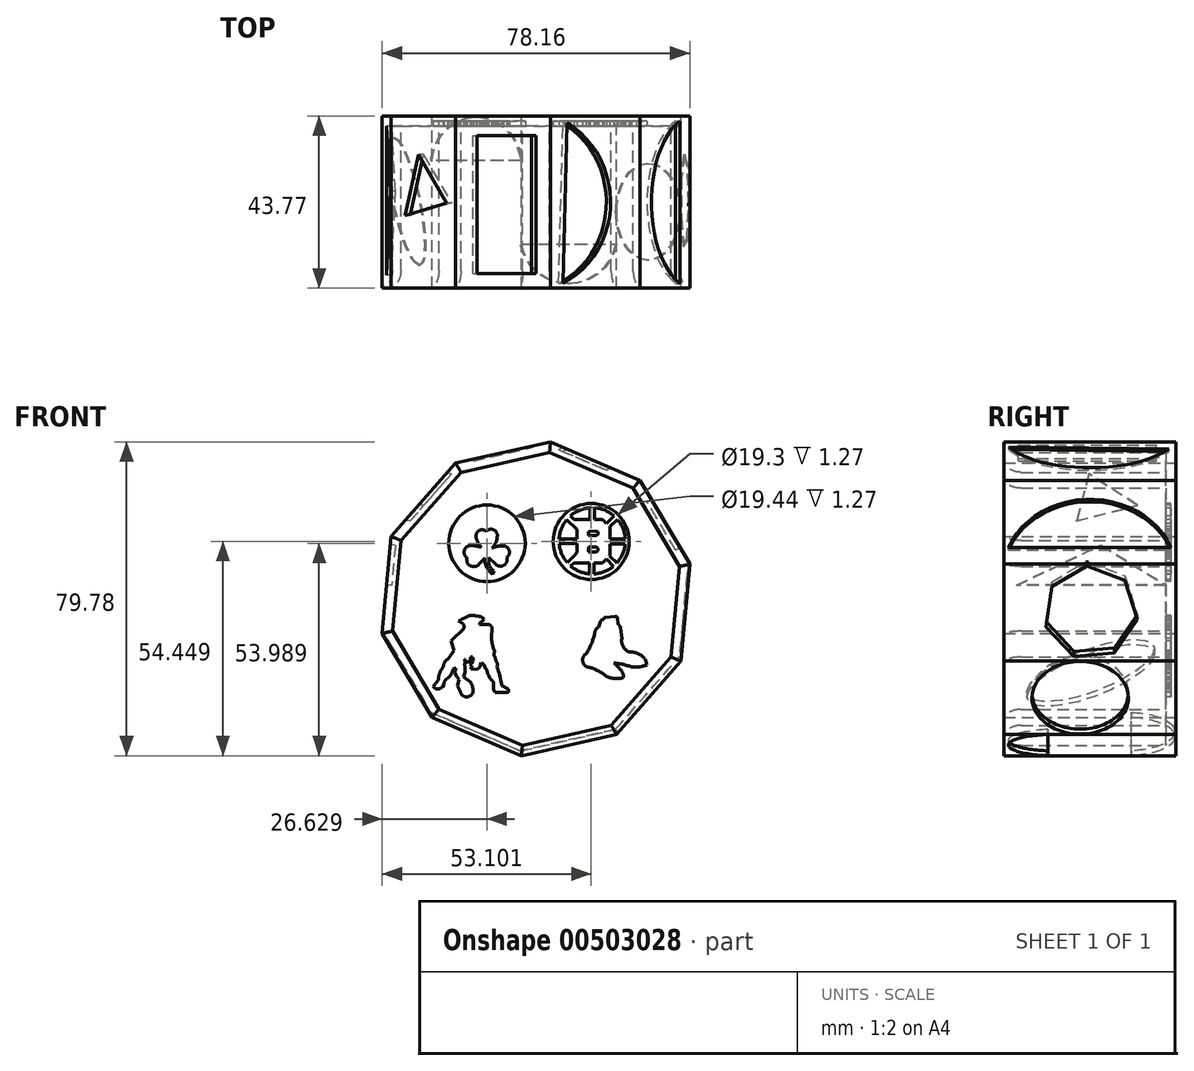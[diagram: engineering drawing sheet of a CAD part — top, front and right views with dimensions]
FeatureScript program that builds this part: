
annotation { "Feature Type Name" : "Feature", "Feature Type Description" : "" }
export const myFeature = defineFeature(function(context is Context, id is Id, definition is map)
    precondition{}
    {
        {
            var Q0;
            Q0=qCreatedBy(makeId("Front.planeOp"),FACE);
            var sketch = newSketch(context, id + "F0", { "sketchPlane" : qUnion([Q0])});
            skCircle(sketch, "E0.cCircle", {"center": v(0, 0) * mm, "radius": 38.1 * mm, "construction": true});
            skLineSegment(sketch, "E0.0", {"start": v(3.7, 39.89) * mm, "end": v(26.44, 30.1) * mm});
            skLineSegment(sketch, "E0.1", {"start": v(26.44, 30.1) * mm, "end": v(39.08, 8.8) * mm});
            skLineSegment(sketch, "E0.2", {"start": v(39.08, 8.8) * mm, "end": v(36.8, -15.85) * mm});
            skLineSegment(sketch, "E0.3", {"start": v(36.8, -15.85) * mm, "end": v(20.45, -34.45) * mm});
            skLineSegment(sketch, "E0.4", {"start": v(20.45, -34.45) * mm, "end": v(-3.7, -39.89) * mm});
            skLineSegment(sketch, "E0.5", {"start": v(-3.7, -39.89) * mm, "end": v(-26.44, -30.1) * mm});
            skLineSegment(sketch, "E0.6", {"start": v(-26.44, -30.1) * mm, "end": v(-39.08, -8.8) * mm});
            skLineSegment(sketch, "E0.7", {"start": v(-39.08, -8.8) * mm, "end": v(-36.8, 15.85) * mm});
            skLineSegment(sketch, "E0.8", {"start": v(-36.8, 15.85) * mm, "end": v(-20.45, 34.45) * mm});
            skLineSegment(sketch, "E0.9", {"start": v(-20.45, 34.45) * mm, "end": v(3.7, 39.89) * mm});
            skPoint(sketch, "E0.0.midPoint", {"position": v(15.07, 35) * mm});
            skSolve(sketch);
        }
        {
            var Q0;
            Q0 = qSketchRegion(id + "F0", true);
            extrude(context, id + "F1", {"entities" : qUnion([Q0]), "depth" : 25.4 * mm, "hasSecondDirection" : true, "secondDirectionOppositeDirection" : true, "secondDirectionDepth" : 12.7 * mm});
        }
        {
            var Q0;
            Q0 = qSketchRegion(id + "F0", true);
            extrude(context, id + "F2", {"entities" : qUnion([Q0]), "operationType" : NewBodyOperationType.ADD, "oppositeDirection" : true, "depth" : 19.05 * mm});
        }
        {
            var Q0;
            Q0=makeQuery(id+"F1.opExtrude","CAP_FACE",FACE,{"disambiguationData":[OSD([sQuery(id+"F0.wireOp",EDGE,"E0.0"),sQuery(id+"F0.wireOp",EDGE,"E0.1"),sQuery(id+"F0.wireOp",EDGE,"E0.2"),sQuery(id+"F0.wireOp",EDGE,"E0.3"),sQuery(id+"F0.wireOp",EDGE,"E0.4"),sQuery(id+"F0.wireOp",EDGE,"E0.5"),sQuery(id+"F0.wireOp",EDGE,"E0.6"),sQuery(id+"F0.wireOp",EDGE,"E0.7"),sQuery(id+"F0.wireOp",EDGE,"E0.8"),sQuery(id+"F0.wireOp",EDGE,"E0.9")])],"isStart":false});
            shell(context, id + "F3", {"entities" : qUnion([Q0]), "thickness" : 2.54 * mm});
        }
        {
            var Q0;
            {var subQ0=sQuery(id+"F0.wireOp",EDGE,"E0.1");Q0=makeQuery(id+"F3.opShell","OFFSET_EDGE",EDGE,{"disambiguationData":[OSD([subQ0]),TDD([makeQuery(id+"F1.opExtrude","CAP_EDGE",EDGE,{"disambiguationData":[OSD([subQ0])],"isStart":false})])]});}
            var Q1;
            {var subQ0=sQuery(id+"F0.wireOp",EDGE,"E0.2");Q1=makeQuery(id+"F3.opShell","OFFSET_EDGE",EDGE,{"disambiguationData":[OSD([subQ0]),TDD([makeQuery(id+"F1.opExtrude","CAP_EDGE",EDGE,{"disambiguationData":[OSD([subQ0])],"isStart":false})])]});}
            var Q2;
            {var subQ0=sQuery(id+"F0.wireOp",EDGE,"E0.3");Q2=makeQuery(id+"F3.opShell","OFFSET_EDGE",EDGE,{"disambiguationData":[OSD([subQ0]),TDD([makeQuery(id+"F1.opExtrude","CAP_EDGE",EDGE,{"disambiguationData":[OSD([subQ0])],"isStart":false})])]});}
            var Q3;
            {var subQ0=sQuery(id+"F0.wireOp",EDGE,"E0.4");Q3=makeQuery(id+"F3.opShell","OFFSET_EDGE",EDGE,{"disambiguationData":[OSD([subQ0]),TDD([makeQuery(id+"F1.opExtrude","CAP_EDGE",EDGE,{"disambiguationData":[OSD([subQ0])],"isStart":false})])]});}
            var Q4;
            {var subQ0=sQuery(id+"F0.wireOp",EDGE,"E0.5");Q4=makeQuery(id+"F3.opShell","OFFSET_EDGE",EDGE,{"disambiguationData":[OSD([subQ0]),TDD([makeQuery(id+"F1.opExtrude","CAP_EDGE",EDGE,{"disambiguationData":[OSD([subQ0])],"isStart":false})])]});}
            var Q5;
            {var subQ0=sQuery(id+"F0.wireOp",EDGE,"E0.0");Q5=makeQuery(id+"F3.opShell","OFFSET_EDGE",EDGE,{"disambiguationData":[OSD([subQ0]),TDD([makeQuery(id+"F1.opExtrude","CAP_EDGE",EDGE,{"disambiguationData":[OSD([subQ0])],"isStart":false})])]});}
            var Q6;
            {var subQ0=sQuery(id+"F0.wireOp",EDGE,"E0.9");Q6=makeQuery(id+"F3.opShell","OFFSET_EDGE",EDGE,{"disambiguationData":[OSD([subQ0]),TDD([makeQuery(id+"F1.opExtrude","CAP_EDGE",EDGE,{"disambiguationData":[OSD([subQ0])],"isStart":false})])]});}
            var Q7;
            {var subQ0=sQuery(id+"F0.wireOp",EDGE,"E0.8");Q7=makeQuery(id+"F3.opShell","OFFSET_EDGE",EDGE,{"disambiguationData":[OSD([subQ0]),TDD([makeQuery(id+"F1.opExtrude","CAP_EDGE",EDGE,{"disambiguationData":[OSD([subQ0])],"isStart":false})])]});}
            var Q8;
            {var subQ0=sQuery(id+"F0.wireOp",EDGE,"E0.7");Q8=makeQuery(id+"F3.opShell","OFFSET_EDGE",EDGE,{"disambiguationData":[OSD([subQ0]),TDD([makeQuery(id+"F1.opExtrude","CAP_EDGE",EDGE,{"disambiguationData":[OSD([subQ0])],"isStart":false})])]});}
            var Q9;
            {var subQ0=sQuery(id+"F0.wireOp",EDGE,"E0.6");Q9=makeQuery(id+"F3.opShell","OFFSET_EDGE",EDGE,{"disambiguationData":[OSD([subQ0]),TDD([makeQuery(id+"F1.opExtrude","CAP_EDGE",EDGE,{"disambiguationData":[OSD([subQ0])],"isStart":false})])]});}
            fillet(context, id + "F4", {"entities" : qUnion([Q0, Q1, Q2, Q3, Q4, Q5, Q6, Q7, Q8, Q9]), "radius" : 5.08 * mm, "tangentPropagation" : true, "allowEdgeOverflow" : false});
        }
        {
            var Q0;
            Q0=makeQuery(id+"F3.opShell","OFFSET_FACE",FACE,{"disambiguationData":[OSD([sQuery(id+"F0.wireOp",EDGE,"E0.0"),sQuery(id+"F0.wireOp",EDGE,"E0.1"),sQuery(id+"F0.wireOp",EDGE,"E0.2"),sQuery(id+"F0.wireOp",EDGE,"E0.3"),sQuery(id+"F0.wireOp",EDGE,"E0.4"),sQuery(id+"F0.wireOp",EDGE,"E0.5"),sQuery(id+"F0.wireOp",EDGE,"E0.6"),sQuery(id+"F0.wireOp",EDGE,"E0.7"),sQuery(id+"F0.wireOp",EDGE,"E0.8"),sQuery(id+"F0.wireOp",EDGE,"E0.9")])]});
            var sketch = newSketch(context, id + "F5", { "sketchPlane" : qUnion([Q0])});
            skCircle(sketch, "E1", {"center": v(-12.45, 14.1) * mm, "radius": 9.72 * mm});
            skPoint(sketch, "E1.first.point", {"position": v(-12.45, 4.38) * mm});
            skPoint(sketch, "E1.first.point.positionSnap0", {"position": v(-12.45, 3.33) * mm});
            skPoint(sketch, "E1.second.point", {"position": v(-12.45, 23.82) * mm});
            skPoint(sketch, "E1.second.point.positionSnap0", {"position": v(-12.45, 3.33) * mm});
            skPoint(sketch, "E1.third.point", {"position": v(-6.09, 21.45) * mm});
            skArc(sketch, "E2", {"start": v(-12.96, 10.41) * mm, "mid": v(-12.53, 8.05) * mm, "end": v(-11, 6.21) * mm});
            skArc(sketch, "E3", {"start": v(-12.12, 10.54) * mm, "mid": v(-11.9, 8.6) * mm, "end": v(-10.73, 7.03) * mm});
            skLineSegment(sketch, "E4", {"start": v(-10.73, 7.03) * mm, "end": v(-11, 6.21) * mm});
            skLineSegment(sketch, "E5", {"start": v(-12.12, 10.54) * mm, "end": v(-10.2, 8.72) * mm});
            skLineSegment(sketch, "E6", {"start": v(-12.96, 10.41) * mm, "end": v(-14.56, 8.72) * mm});
            skArc(sketch, "E7", {"start": v(-10.2, 8.72) * mm, "mid": v(-8.14, 8.53) * mm, "end": v(-7.46, 10.49) * mm});
            skArc(sketch, "E8", {"start": v(-7.46, 10.49) * mm, "mid": v(-6.8, 12.25) * mm, "end": v(-8.24, 13.46) * mm});
            skArc(sketch, "E9", {"start": v(-17.53, 10.41) * mm, "mid": v(-16.7, 8.4) * mm, "end": v(-14.56, 8.72) * mm});
            skArc(sketch, "E10", {"start": v(-16.68, 13.54) * mm, "mid": v(-18.21, 12.28) * mm, "end": v(-17.53, 10.41) * mm});
            skArc(sketch, "E11", {"start": v(-13.8, 13.06) * mm, "mid": v(-15.22, 13.4) * mm, "end": v(-16.68, 13.54) * mm});
            skArc(sketch, "E12", {"start": v(-8.24, 13.46) * mm, "mid": v(-9.78, 13.35) * mm, "end": v(-11.24, 12.85) * mm});
            skArc(sketch, "E13", {"start": v(-11.24, 12.85) * mm, "mid": v(-10.25, 14.25) * mm, "end": v(-9.83, 15.9) * mm});
            skArc(sketch, "E14", {"start": v(-9.83, 15.9) * mm, "mid": v(-10.78, 17.54) * mm, "end": v(-12.63, 17.13) * mm});
            skArc(sketch, "E15", {"start": v(-12.63, 17.13) * mm, "mid": v(-14.36, 17.4) * mm, "end": v(-15.25, 15.9) * mm});
            skArc(sketch, "E16", {"start": v(-15.25, 15.9) * mm, "mid": v(-14.78, 14.35) * mm, "end": v(-13.8, 13.06) * mm});
            skCircle(sketch, "E17", {"center": v(14.02, 14.56) * mm, "radius": 9.65 * mm});
            skPoint(sketch, "E17.first.point", {"position": v(14.6, 4.92) * mm});
            skPoint(sketch, "E17.second.point", {"position": v(14.21, 24.2) * mm});
            skPoint(sketch, "E17.second.point.positionSnap0", {"position": v(14.21, 24.72) * mm});
            skPoint(sketch, "E17.third.point", {"position": v(9.59, 23.13) * mm});
            skArc(sketch, "E18", {"start": v(7.8, 20.1) * mm, "mid": v(6.44, 17.82) * mm, "end": v(5.86, 15.22) * mm});
            skPoint(sketch, "E18.first.point", {"position": v(14.35, 6.3) * mm});
            skPoint(sketch, "E18.second.point", {"position": v(14.02, 23.13) * mm});
            skPoint(sketch, "E18.third.point", {"position": v(9.59, 21.72) * mm});
            skLineSegment(sketch, "E19", {"start": v(10.13, 20.2) * mm, "end": v(9.62, 20.2) * mm});
            skLineSegment(sketch, "E20", {"start": v(9.62, 18.37) * mm, "end": v(10.39, 17.63) * mm});
            skLineSegment(sketch, "E21", {"start": v(9.62, 10.82) * mm, "end": v(10.4, 11.72) * mm});
            skLineSegment(sketch, "E22", {"start": v(9.62, 10.82) * mm, "end": v(7.93, 9.18) * mm});
            skLineSegment(sketch, "E23", {"start": v(9.62, 9.13) * mm, "end": v(13.6, 9.13) * mm});
            skLineSegment(sketch, "E24", {"start": v(8.76, 8.35) * mm, "end": v(9.62, 9.13) * mm});
            skLineSegment(sketch, "E25", {"start": v(13.6, 9.13) * mm, "end": v(13.6, 6.33) * mm});
            skLineSegment(sketch, "E26", {"start": v(14.78, 9.13) * mm, "end": v(14.78, 6.3) * mm});
            skLineSegment(sketch, "E27", {"start": v(14.78, 9.13) * mm, "end": v(16.9, 9.13) * mm});
            skLineSegment(sketch, "E28", {"start": v(16.9, 9.13) * mm, "end": v(17.87, 10.09) * mm});
            skLineSegment(sketch, "E29", {"start": v(17.87, 10.09) * mm, "end": v(19.68, 8.28) * mm});
            skLineSegment(sketch, "E30", {"start": v(20.59, 9.16) * mm, "end": v(18.72, 10.83) * mm});
            skLineSegment(sketch, "E31", {"start": v(18.72, 10.83) * mm, "end": v(18.82, 11.3) * mm});
            skLineSegment(sketch, "E32", {"start": v(18.82, 11.3) * mm, "end": v(18.82, 13.9) * mm});
            skLineSegment(sketch, "E33", {"start": v(18.82, 13.9) * mm, "end": v(18.3, 14.52) * mm});
            skLineSegment(sketch, "E34", {"start": v(18.3, 14.52) * mm, "end": v(18.82, 15.24) * mm});
            skLineSegment(sketch, "E35", {"start": v(18.82, 15.24) * mm, "end": v(22.67, 15.24) * mm});
            skLineSegment(sketch, "E36", {"start": v(22.64, 13.9) * mm, "end": v(18.82, 13.9) * mm});
            skLineSegment(sketch, "E37", {"start": v(18.82, 15.24) * mm, "end": v(18.82, 18.34) * mm});
            skLineSegment(sketch, "E38", {"start": v(18.82, 18.34) * mm, "end": v(20.66, 20.2) * mm});
            skLineSegment(sketch, "E39", {"start": v(17.96, 19.18) * mm, "end": v(16.9, 20.2) * mm});
            skLineSegment(sketch, "E40", {"start": v(17.96, 19.18) * mm, "end": v(19.77, 21.09) * mm});
            skLineSegment(sketch, "E41", {"start": v(10.13, 20.2) * mm, "end": v(13.67, 20.2) * mm});
            skLineSegment(sketch, "E42", {"start": v(13.67, 20.2) * mm, "end": v(13.67, 23.11) * mm});
            skLineSegment(sketch, "E43", {"start": v(14.83, 20.2) * mm, "end": v(14.83, 23.12) * mm});
            skLineSegment(sketch, "E44", {"start": v(14.83, 20.2) * mm, "end": v(16.9, 20.2) * mm});
            skLineSegment(sketch, "E45", {"start": v(10.4, 11.72) * mm, "end": v(10.4, 14) * mm});
            skLineSegment(sketch, "E46", {"start": v(10.4, 14) * mm, "end": v(5.88, 14) * mm});
            skLineSegment(sketch, "E47", {"start": v(10.39, 17.63) * mm, "end": v(10.39, 15.22) * mm});
            skLineSegment(sketch, "E48", {"start": v(10.39, 15.22) * mm, "end": v(5.86, 15.22) * mm});
            skLineSegment(sketch, "E49", {"start": v(9.62, 18.37) * mm, "end": v(7.8, 20.1) * mm});
            skLineSegment(sketch, "E50", {"start": v(9.62, 20.2) * mm, "end": v(8.75, 21.08) * mm});
            skLineSegment(sketch, "E51", {"start": v(13.3, 17.14) * mm, "end": v(13.3, 16.12) * mm});
            skLineSegment(sketch, "E52", {"start": v(13.3, 16.12) * mm, "end": v(15.37, 16.12) * mm});
            skLineSegment(sketch, "E53", {"start": v(15.37, 16.12) * mm, "end": v(15.68, 16.34) * mm});
            skLineSegment(sketch, "E54", {"start": v(15.68, 16.34) * mm, "end": v(15.68, 16.92) * mm});
            skLineSegment(sketch, "E55", {"start": v(15.68, 16.92) * mm, "end": v(15.37, 17.17) * mm});
            skLineSegment(sketch, "E56", {"start": v(15.37, 17.17) * mm, "end": v(13.3, 17.14) * mm});
            skLineSegment(sketch, "E57", {"start": v(13.3, 13.11) * mm, "end": v(13.3, 11.92) * mm});
            skLineSegment(sketch, "E58", {"start": v(13.3, 11.92) * mm, "end": v(15.37, 11.92) * mm});
            skLineSegment(sketch, "E59", {"start": v(15.37, 11.92) * mm, "end": v(15.7, 12.24) * mm});
            skLineSegment(sketch, "E60", {"start": v(15.7, 12.24) * mm, "end": v(15.7, 12.8) * mm});
            skLineSegment(sketch, "E61", {"start": v(15.7, 12.8) * mm, "end": v(15.37, 13.11) * mm});
            skLineSegment(sketch, "E62", {"start": v(15.37, 13.11) * mm, "end": v(13.3, 13.11) * mm});
            skArc(sketch, "E63.trimOffspring", {"start": v(13.67, 23.11) * mm, "mid": v(11.05, 22.5) * mm, "end": v(8.75, 21.08) * mm});
            skArc(sketch, "E64.trimOffspring", {"start": v(5.88, 14) * mm, "mid": v(6.52, 11.42) * mm, "end": v(7.93, 9.18) * mm});
            skArc(sketch, "E65.trimOffspring", {"start": v(8.76, 8.35) * mm, "mid": v(11.02, 6.95) * mm, "end": v(13.6, 6.33) * mm});
            skArc(sketch, "E66.trimOffspring", {"start": v(19.77, 21.09) * mm, "mid": v(17.47, 22.5) * mm, "end": v(14.83, 23.12) * mm});
            skArc(sketch, "E67.trimOffspring", {"start": v(22.67, 15.24) * mm, "mid": v(22.07, 17.88) * mm, "end": v(20.66, 20.2) * mm});
            skArc(sketch, "E68.trimOffspring", {"start": v(20.59, 9.16) * mm, "mid": v(21.99, 11.37) * mm, "end": v(22.64, 13.9) * mm});
            skArc(sketch, "E69.trimOffspring", {"start": v(14.78, 6.32) * mm, "mid": v(17.39, 6.9) * mm, "end": v(19.68, 8.28) * mm});
            skLineSegment(sketch, "E70", {"start": v(16.41, -5.7) * mm, "end": v(15.81, -7.24) * mm});
            skArc(sketch, "E71", {"start": v(15.81, -7.24) * mm, "mid": v(15.13, -7.94) * mm, "end": v(14.89, -8.89) * mm});
            skArc(sketch, "E72", {"start": v(12.7, -14.01) * mm, "mid": v(14.03, -11.55) * mm, "end": v(14.89, -8.89) * mm});
            skArc(sketch, "E73", {"start": v(12.7, -14.01) * mm, "mid": v(11.91, -16.14) * mm, "end": v(13.75, -17.45) * mm});
            skArc(sketch, "E74", {"start": v(17.1, -19.09) * mm, "mid": v(15.49, -18.14) * mm, "end": v(13.75, -17.45) * mm});
            skArc(sketch, "E75", {"start": v(17.1, -19.09) * mm, "mid": v(19.53, -20.22) * mm, "end": v(22.2, -19.98) * mm});
            skArc(sketch, "E76", {"start": v(22.2, -19.98) * mm, "mid": v(22.06, -18.92) * mm, "end": v(21.47, -18.04) * mm});
            skArc(sketch, "E77", {"start": v(21.47, -18.04) * mm, "mid": v(20.68, -17.15) * mm, "end": v(19.84, -16.32) * mm});
            skArc(sketch, "E78", {"start": v(24.23, -17.32) * mm, "mid": v(22.07, -16.66) * mm, "end": v(19.84, -16.32) * mm});
            skArc(sketch, "E79", {"start": v(24.23, -17.32) * mm, "mid": v(26.23, -17.31) * mm, "end": v(28.17, -16.79) * mm});
            skArc(sketch, "E80", {"start": v(28.17, -16.79) * mm, "mid": v(27.31, -14.91) * mm, "end": v(25.57, -13.8) * mm});
            skArc(sketch, "E81", {"start": v(25.57, -13.8) * mm, "mid": v(24.78, -13.58) * mm, "end": v(23.95, -13.55) * mm});
            skArc(sketch, "E82", {"start": v(21.8, -10.12) * mm, "mid": v(22.18, -12.27) * mm, "end": v(23.95, -13.55) * mm});
            skLineSegment(sketch, "E83", {"start": v(21.8, -10.12) * mm, "end": v(21.46, -7.43) * mm});
            skArc(sketch, "E84", {"start": v(21.46, -7.43) * mm, "mid": v(21.24, -6.87) * mm, "end": v(20.79, -6.47) * mm});
            skLineSegment(sketch, "E85", {"start": v(20.03, -4.46) * mm, "end": v(17.66, -4.69) * mm});
            skArc(sketch, "E86", {"start": v(17.66, -4.69) * mm, "mid": v(17.35, -4.86) * mm, "end": v(17.25, -5.2) * mm});
            skArc(sketch, "E87", {"start": v(17.25, -5.2) * mm, "mid": v(16.75, -5.31) * mm, "end": v(16.41, -5.7) * mm});
            skArc(sketch, "E88", {"start": v(20.7, -4.8) * mm, "mid": v(20.41, -4.53) * mm, "end": v(20.03, -4.46) * mm});
            skLineSegment(sketch, "E89", {"start": v(20.7, -4.8) * mm, "end": v(20.79, -6.47) * mm});
            skArc(sketch, "E90", {"start": v(-19.24, -23.65) * mm, "mid": v(-17.11, -24.86) * mm, "end": v(-16.08, -22.63) * mm});
            skArc(sketch, "E91", {"start": v(-16.08, -22.63) * mm, "mid": v(-16.21, -22.05) * mm, "end": v(-16.56, -21.56) * mm});
            skLineSegment(sketch, "E92", {"start": v(-18.45, -19.84) * mm, "end": v(-16.56, -21.24) * mm});
            skLineSegment(sketch, "E93", {"start": v(-16.56, -21.56) * mm, "end": v(-16.56, -21.24) * mm});
            skLineSegment(sketch, "E94", {"start": v(-18.45, -19.84) * mm, "end": v(-18.07, -18.71) * mm});
            skLineSegment(sketch, "E95", {"start": v(-18.07, -18.71) * mm, "end": v(-18.07, -17.04) * mm});
            skArc(sketch, "E96", {"start": v(-18.07, -16.5) * mm, "mid": v(-18.2, -16.77) * mm, "end": v(-18.07, -17.04) * mm});
            skArc(sketch, "E97", {"start": v(-18.07, -16.5) * mm, "mid": v(-18.03, -15.8) * mm, "end": v(-18.33, -15.16) * mm});
            skLineSegment(sketch, "E98", {"start": v(-18.17, -15.41) * mm, "end": v(-18.06, -15.41) * mm});
            skLineSegment(sketch, "E99", {"start": v(-18.06, -15.41) * mm, "end": v(-17.86, -16.04) * mm});
            skLineSegment(sketch, "E100", {"start": v(-17.86, -16.04) * mm, "end": v(-16.76, -16.08) * mm});
            skLineSegment(sketch, "E101", {"start": v(-16.76, -16.08) * mm, "end": v(-16.64, -14.71) * mm});
            skLineSegment(sketch, "E102", {"start": v(-16.64, -14.71) * mm, "end": v(-16.11, -14.73) * mm});
            skLineSegment(sketch, "E103", {"start": v(-16.11, -14.73) * mm, "end": v(-15.83, -15.84) * mm});
            skLineSegment(sketch, "E104", {"start": v(-15.83, -15.84) * mm, "end": v(-16.7, -16.75) * mm});
            skLineSegment(sketch, "E105", {"start": v(-16.7, -16.75) * mm, "end": v(-16.7, -16.99) * mm});
            skLineSegment(sketch, "E106", {"start": v(-16.7, -16.99) * mm, "end": v(-16.26, -16.99) * mm});
            skLineSegment(sketch, "E107", {"start": v(-16.26, -16.99) * mm, "end": v(-16.54, -17.63) * mm});
            skLineSegment(sketch, "E108", {"start": v(-16.54, -17.63) * mm, "end": v(-16.54, -17.83) * mm});
            skLineSegment(sketch, "E109", {"start": v(-16.54, -17.83) * mm, "end": v(-14.98, -17.98) * mm});
            skLineSegment(sketch, "E110", {"start": v(-14.98, -17.98) * mm, "end": v(-14.26, -17.3) * mm});
            skLineSegment(sketch, "E111", {"start": v(-14.26, -17.3) * mm, "end": v(-14.2, -16.99) * mm});
            skLineSegment(sketch, "E112", {"start": v(-14.2, -16.99) * mm, "end": v(-13.82, -16.36) * mm});
            skLineSegment(sketch, "E113", {"start": v(-13.82, -16.36) * mm, "end": v(-13.62, -16.42) * mm});
            skLineSegment(sketch, "E114", {"start": v(-13.62, -16.42) * mm, "end": v(-13.03, -16.99) * mm});
            skLineSegment(sketch, "E115", {"start": v(-13.03, -16.99) * mm, "end": v(-12.95, -17.59) * mm});
            skLineSegment(sketch, "E116", {"start": v(-12.95, -17.59) * mm, "end": v(-12.47, -18.05) * mm});
            skArc(sketch, "E117", {"start": v(-12.47, -18.05) * mm, "mid": v(-11.9, -19.79) * mm, "end": v(-10.74, -21.2) * mm});
            skLineSegment(sketch, "E118", {"start": v(-10.74, -21.2) * mm, "end": v(-10.74, -23.08) * mm});
            skLineSegment(sketch, "E119", {"start": v(-10.74, -23.08) * mm, "end": v(-10.37, -23.77) * mm});
            skLineSegment(sketch, "E120", {"start": v(-10.37, -23.77) * mm, "end": v(-7.13, -23.77) * mm});
            skArc(sketch, "E121", {"start": v(-7.13, -23.77) * mm, "mid": v(-6.95, -23.36) * mm, "end": v(-7.13, -22.96) * mm});
            skLineSegment(sketch, "E122", {"start": v(-7.13, -22.96) * mm, "end": v(-8.72, -22.06) * mm});
            skArc(sketch, "E123", {"start": v(-8.72, -22.06) * mm, "mid": v(-9.17, -19.68) * mm, "end": v(-9.94, -17.38) * mm});
            skLineSegment(sketch, "E124", {"start": v(-9.94, -17.38) * mm, "end": v(-9.73, -16.72) * mm});
            skArc(sketch, "E125", {"start": v(-10.44, -14.73) * mm, "mid": v(-10.14, -15.74) * mm, "end": v(-9.73, -16.72) * mm});
            skArc(sketch, "E126", {"start": v(-10.44, -14.73) * mm, "mid": v(-11.29, -14.19) * mm, "end": v(-12.24, -14.49) * mm});
            skArc(sketch, "E127", {"start": v(-10.44, -13.45) * mm, "mid": v(-10.68, -13.93) * mm, "end": v(-10.67, -14.47) * mm});
            skArc(sketch, "E128", {"start": v(-11.27, -9.18) * mm, "mid": v(-11.15, -11.37) * mm, "end": v(-10.44, -13.45) * mm});
            skLineSegment(sketch, "E129", {"start": v(-11.27, -9.18) * mm, "end": v(-11.18, -8.06) * mm});
            skArc(sketch, "E130", {"start": v(-11.18, -8.06) * mm, "mid": v(-11.48, -6.86) * mm, "end": v(-12.67, -6.52) * mm});
            skLineSegment(sketch, "E131", {"start": v(-12.67, -6.52) * mm, "end": v(-14.3, -6.52) * mm});
            skLineSegment(sketch, "E132", {"start": v(-14.3, -6.52) * mm, "end": v(-14.3, -6.28) * mm});
            skLineSegment(sketch, "E133", {"start": v(-14.3, -6.28) * mm, "end": v(-13.2, -5.22) * mm});
            skArc(sketch, "E134", {"start": v(-13.2, -5.22) * mm, "mid": v(-14, -4.6) * mm, "end": v(-15.02, -4.44) * mm});
            skArc(sketch, "E135", {"start": v(-15.02, -4.44) * mm, "mid": v(-16.48, -4.2) * mm, "end": v(-17.85, -4.75) * mm});
            skArc(sketch, "E136", {"start": v(-17.85, -4.75) * mm, "mid": v(-18.78, -5.16) * mm, "end": v(-19.66, -5.65) * mm});
            skArc(sketch, "E137", {"start": v(-18.26, -6.74) * mm, "mid": v(-18.9, -6.13) * mm, "end": v(-19.66, -5.65) * mm});
            skLineSegment(sketch, "E138", {"start": v(-18.26, -6.74) * mm, "end": v(-18.26, -7.53) * mm});
            skLineSegment(sketch, "E139", {"start": v(-18.26, -7.53) * mm, "end": v(-21.61, -10.76) * mm});
            skLineSegment(sketch, "E140", {"start": v(-21.61, -10.76) * mm, "end": v(-20.89, -13.1) * mm});
            skLineSegment(sketch, "E141", {"start": v(-20.89, -13.1) * mm, "end": v(-22.18, -15.16) * mm});
            skArc(sketch, "E142", {"start": v(-22.18, -15.16) * mm, "mid": v(-23.19, -16.11) * mm, "end": v(-23.58, -17.44) * mm});
            skArc(sketch, "E143", {"start": v(-23.58, -17.44) * mm, "mid": v(-24.52, -18.92) * mm, "end": v(-24.72, -20.67) * mm});
            skLineSegment(sketch, "E144", {"start": v(-24.72, -20.67) * mm, "end": v(-26.15, -22.34) * mm});
            skArc(sketch, "E145", {"start": v(-26.18, -22.24) * mm, "mid": v(-25.03, -22.91) * mm, "end": v(-23.82, -22.34) * mm});
            skLineSegment(sketch, "E146", {"start": v(-23.82, -22.34) * mm, "end": v(-23.4, -21.77) * mm});
            skArc(sketch, "E147", {"start": v(-22.45, -20.2) * mm, "mid": v(-23.15, -20.85) * mm, "end": v(-23.4, -21.77) * mm});
            skArc(sketch, "E148", {"start": v(-22.45, -20.2) * mm, "mid": v(-21.54, -19.13) * mm, "end": v(-21.05, -17.8) * mm});
            skLineSegment(sketch, "E149", {"start": v(-21.05, -17.8) * mm, "end": v(-20.32, -17.62) * mm});
            skLineSegment(sketch, "E150", {"start": v(-20.32, -17.62) * mm, "end": v(-20.75, -18.67) * mm});
            skLineSegment(sketch, "E151", {"start": v(-20.75, -18.67) * mm, "end": v(-20.08, -19.84) * mm});
            skLineSegment(sketch, "E152", {"start": v(-20.08, -19.84) * mm, "end": v(-19.62, -20.47) * mm});
            skLineSegment(sketch, "E153", {"start": v(-19.62, -20.47) * mm, "end": v(-19.98, -22.17) * mm});
            skLineSegment(sketch, "E154", {"start": v(-19.98, -22.17) * mm, "end": v(-19.24, -23.65) * mm});
            skSolve(sketch);
        }
        {
            var Q0;
            Q0 = qSketchRegion(id + "F5", true);
            extrude(context, id + "F6", {"entities" : qUnion([Q0]), "operationType" : NewBodyOperationType.REMOVE, "oppositeDirection" : true, "depth" : 1.27 * mm});
        }
        {
            var Q0;
            {var subQ0=sQuery(id+"F0.wireOp",EDGE,"E0.4");Q0=makeQuery(id+"F2.boolean.opBoolean","MERGE",FACE,{"derivedFrom":[makeQuery(id+"F1.opExtrude","SWEPT_FACE",FACE,{"disambiguationData":[OSD([subQ0])]}),makeQuery(id+"F2.opExtrude","SWEPT_FACE",FACE,{"disambiguationData":[OSD([subQ0])]})]});}
            var sketch = newSketch(context, id + "F7", { "sketchPlane" : qUnion([Q0])});
            skArc(sketch, "E155", {"start": v(12.38, 13.42) * mm, "mid": v(0, 23.54) * mm, "end": v(-12.38, 13.42) * mm});
            skLineSegment(sketch, "E156", {"start": v(-12.38, 13.42) * mm, "end": v(12.38, 13.42) * mm});
            skSolve(sketch);
        }
        {
            var Q0;
            {var subQ0=sQuery(id+"F0.wireOp",EDGE,"E0.3");Q0=makeQuery(id+"F2.boolean.opBoolean","MERGE",FACE,{"derivedFrom":[makeQuery(id+"F1.opExtrude","SWEPT_FACE",FACE,{"disambiguationData":[OSD([subQ0])]}),makeQuery(id+"F2.opExtrude","SWEPT_FACE",FACE,{"disambiguationData":[OSD([subQ0])]})]});}
            var sketch = newSketch(context, id + "F8", { "sketchPlane" : qUnion([Q0])});
            skCircle(sketch, "E157", {"center": v(-5.27, 0) * mm, "radius": 12.27 * mm});
            skSolve(sketch);
        }
        {
            var Q0;
            {var subQ0=sQuery(id+"F0.wireOp",EDGE,"E0.2");Q0=makeQuery(id+"F2.boolean.opBoolean","MERGE",FACE,{"derivedFrom":[makeQuery(id+"F1.opExtrude","SWEPT_FACE",FACE,{"disambiguationData":[OSD([subQ0])]}),makeQuery(id+"F2.opExtrude","SWEPT_FACE",FACE,{"disambiguationData":[OSD([subQ0])]})]});}
            var sketch = newSketch(context, id + "F9", { "sketchPlane" : qUnion([Q0])});
            skCircle(sketch, "E158.cCircle", {"center": v(-2.58, 0) * mm, "radius": 10.74 * mm, "construction": true});
            skLineSegment(sketch, "E158.0", {"start": v(-13.94, -3.6) * mm, "end": v(-12.47, 6.64) * mm});
            skLineSegment(sketch, "E158.1", {"start": v(-12.47, 6.64) * mm, "end": v(-3.56, 11.88) * mm});
            skLineSegment(sketch, "E158.2", {"start": v(-3.56, 11.88) * mm, "end": v(6.1, 8.17) * mm});
            skLineSegment(sketch, "E158.3", {"start": v(6.1, 8.17) * mm, "end": v(9.22, -1.69) * mm});
            skLineSegment(sketch, "E158.4", {"start": v(9.22, -1.69) * mm, "end": v(3.46, -10.28) * mm});
            skLineSegment(sketch, "E158.5", {"start": v(3.46, -10.28) * mm, "end": v(-6.85, -11.12) * mm});
            skLineSegment(sketch, "E158.6", {"start": v(-6.85, -11.12) * mm, "end": v(-13.94, -3.6) * mm});
            skPoint(sketch, "E158.0.midPoint", {"position": v(-13.2, 1.52) * mm});
            skSolve(sketch);
        }
        {
            var Q0;
            {var subQ0=sQuery(id+"F0.wireOp",EDGE,"E0.1");Q0=makeQuery(id+"F2.boolean.opBoolean","MERGE",FACE,{"derivedFrom":[makeQuery(id+"F1.opExtrude","SWEPT_FACE",FACE,{"disambiguationData":[OSD([subQ0])]}),makeQuery(id+"F2.opExtrude","SWEPT_FACE",FACE,{"disambiguationData":[OSD([subQ0])]})]});}
            var sketch = newSketch(context, id + "F10", { "sketchPlane" : qUnion([Q0])});
            skArc(sketch, "E159", {"start": v(17.8, -7.44) * mm, "mid": v(-2.83, 6.79) * mm, "end": v(-23.47, -7.44) * mm});
            skLineSegment(sketch, "E160", {"start": v(-23.47, -7.44) * mm, "end": v(17.8, -7.44) * mm});
            skSolve(sketch);
        }
        {
            var Q0;
            {var subQ0=sQuery(id+"F0.wireOp",EDGE,"E0.0");Q0=makeQuery(id+"F2.boolean.opBoolean","MERGE",FACE,{"derivedFrom":[makeQuery(id+"F1.opExtrude","SWEPT_FACE",FACE,{"disambiguationData":[OSD([subQ0])]}),makeQuery(id+"F2.opExtrude","SWEPT_FACE",FACE,{"disambiguationData":[OSD([subQ0])]})]});}
            var sketch = newSketch(context, id + "F11", { "sketchPlane" : qUnion([Q0])});
            skArc(sketch, "E161", {"start": v(-8.94, -23.45) * mm, "mid": v(4.2, -3.48) * mm, "end": v(-7.78, 17.2) * mm});
            skLineSegment(sketch, "E162", {"start": v(-8.94, -23.45) * mm, "end": v(-7.78, 17.2) * mm});
            skSolve(sketch);
        }
        {
            var Q0;
            {var subQ0=sQuery(id+"F0.wireOp",EDGE,"E0.9");Q0=makeQuery(id+"F2.boolean.opBoolean","MERGE",FACE,{"derivedFrom":[makeQuery(id+"F1.opExtrude","SWEPT_FACE",FACE,{"disambiguationData":[OSD([subQ0])]}),makeQuery(id+"F2.opExtrude","SWEPT_FACE",FACE,{"disambiguationData":[OSD([subQ0])]})]});}
            var sketch = newSketch(context, id + "F12", { "sketchPlane" : qUnion([Q0])});
            skLineSegment(sketch, "E163.bottom", {"start": v(-6.77, -20.98) * mm, "end": v(8.56, -20.98) * mm});
            skLineSegment(sketch, "E163.top", {"start": v(-6.77, 14.08) * mm, "end": v(8.56, 14.08) * mm});
            skLineSegment(sketch, "E163.left", {"start": v(-6.77, -20.98) * mm, "end": v(-6.77, 14.08) * mm});
            skLineSegment(sketch, "E163.right", {"start": v(8.56, -20.98) * mm, "end": v(8.56, 14.08) * mm});
            skSolve(sketch);
        }
        {
            var Q0;
            {var subQ0=sQuery(id+"F0.wireOp",EDGE,"E0.8");Q0=makeQuery(id+"F2.boolean.opBoolean","MERGE",FACE,{"derivedFrom":[makeQuery(id+"F1.opExtrude","SWEPT_FACE",FACE,{"disambiguationData":[OSD([subQ0])]}),makeQuery(id+"F2.opExtrude","SWEPT_FACE",FACE,{"disambiguationData":[OSD([subQ0])]})]});}
            var sketch = newSketch(context, id + "F13", { "sketchPlane" : qUnion([Q0])});
            skCircle(sketch, "E164.cCircle", {"center": v(0, 0) * mm, "radius": 4.7 * mm, "construction": true});
            skLineSegment(sketch, "E164.0", {"start": v(-9.2, -1.83) * mm, "end": v(3.02, 8.88) * mm});
            skLineSegment(sketch, "E164.1", {"start": v(3.02, 8.88) * mm, "end": v(6.18, -7.06) * mm});
            skLineSegment(sketch, "E164.2", {"start": v(6.18, -7.06) * mm, "end": v(-9.2, -1.83) * mm});
            skPoint(sketch, "E164.0.midPoint", {"position": v(-3.1, 3.53) * mm});
            skSolve(sketch);
        }
        {
            var Q0;
            {var subQ0=sQuery(id+"F0.wireOp",EDGE,"E0.7");Q0=makeQuery(id+"F2.boolean.opBoolean","MERGE",FACE,{"derivedFrom":[makeQuery(id+"F1.opExtrude","SWEPT_FACE",FACE,{"disambiguationData":[OSD([subQ0])]}),makeQuery(id+"F2.opExtrude","SWEPT_FACE",FACE,{"disambiguationData":[OSD([subQ0])]})]});}
            var sketch = newSketch(context, id + "F14", { "sketchPlane" : qUnion([Q0])});
            skLineSegment(sketch, "E165", {"start": v(-16.43, 0) * mm, "end": v(21.34, 0) * mm});
            skLineSegment(sketch, "E166", {"start": v(21.34, 0) * mm, "end": v(0, 10.22) * mm});
            skLineSegment(sketch, "E167", {"start": v(0, 10.22) * mm, "end": v(-16.43, 0) * mm});
            skSolve(sketch);
        }
        {
            var Q0;
            {var subQ0=sQuery(id+"F0.wireOp",EDGE,"E0.6");Q0=makeQuery(id+"F2.boolean.opBoolean","MERGE",FACE,{"derivedFrom":[makeQuery(id+"F1.opExtrude","SWEPT_FACE",FACE,{"disambiguationData":[OSD([subQ0])]}),makeQuery(id+"F2.opExtrude","SWEPT_FACE",FACE,{"disambiguationData":[OSD([subQ0])]})]});}
            var sketch = newSketch(context, id + "F15", { "sketchPlane" : qUnion([Q0])});
            skEllipse(sketch, "E168", {"center": v(2.63, 0) * mm, "majorRadius": 17.56 * mm, "minorRadius": 6.12 * mm, "majorAxis": v(-0.9, 0.42)});
            skSolve(sketch);
        }
        {
            var Q0;
            {var subQ0=sQuery(id+"F0.wireOp",EDGE,"E0.5");Q0=makeQuery(id+"F2.boolean.opBoolean","MERGE",FACE,{"derivedFrom":[makeQuery(id+"F1.opExtrude","SWEPT_FACE",FACE,{"disambiguationData":[OSD([subQ0])]}),makeQuery(id+"F2.opExtrude","SWEPT_FACE",FACE,{"disambiguationData":[OSD([subQ0])]})]});}
            var sketch = newSketch(context, id + "F16", { "sketchPlane" : qUnion([Q0])});
            skLineSegment(sketch, "E169", {"start": v(12.38, -7.7) * mm, "end": v(-12.38, -7.7) * mm});
            skArc(sketch, "E170", {"start": v(-12.38, -7.7) * mm, "mid": v(0, -18.8) * mm, "end": v(12.38, -7.7) * mm});
            skSolve(sketch);
        }
        {
            var Q0;
            Q0 = qSketchRegion(id + "F7", true);
            var Q1;
            Q1 = qSketchRegion(id + "F8", true);
            var Q2;
            Q2 = qSketchRegion(id + "F16", true);
            var Q3;
            Q3 = qSketchRegion(id + "F15", true);
            var Q4;
            Q4 = qSketchRegion(id + "F9", true);
            extrude(context, id + "F17", {"entities" : qUnion([Q0, Q1, Q2, Q3, Q4]), "operationType" : NewBodyOperationType.REMOVE, "oppositeDirection" : true, "depth" : 1.27 * mm});
        }
        {
            var Q0;
            Q0 = qSketchRegion(id + "F10", true);
            var Q1;
            Q1 = qSketchRegion(id + "F11", true);
            var Q2;
            Q2 = qSketchRegion(id + "F12", true);
            extrude(context, id + "F18", {"entities" : qUnion([Q0, Q1, Q2]), "operationType" : NewBodyOperationType.REMOVE, "oppositeDirection" : true, "depth" : 1.27 * mm});
        }
        {
            var Q0;
            Q0 = qSketchRegion(id + "F14", true);
            var Q1;
            Q1 = qSketchRegion(id + "F13", true);
            extrude(context, id + "F19", {"entities" : qUnion([Q0, Q1]), "operationType" : NewBodyOperationType.REMOVE, "oppositeDirection" : true, "depth" : 1.27 * mm});
        }
    });
